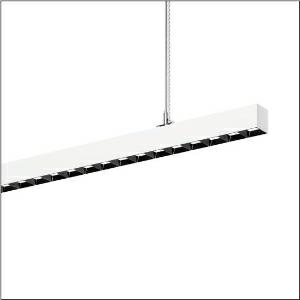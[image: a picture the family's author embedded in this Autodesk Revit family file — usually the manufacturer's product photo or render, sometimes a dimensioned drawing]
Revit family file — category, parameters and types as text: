
# Revit family: silica_r__21_51mx32tat7w_976d
name_source: partatom
category: Lighting Fixtures
units: mm (PartAtom-declared; Revit-internal decimal feet)

## family parameters
Cut with Voids When Loaded = No
Host = Face
Light Source = No
Part Type = Normal
Room Calculation Point = No
Round Connector Dimension = Use Diameter
Shared = No

## types (1)
- --- (1 x LED, 6220 lm, 53.4 W, 6500K)
    Apparent Load = 53 VA
    CIE Flux Codes = 84 99 100 60 100
    Color Rendering = 80
    Color Temperature = 6500K
    Default Elevation = 1800 mm
    Description = Silica® 21, office luminaire, primary light control with darklight reflector, of PMMA, black, CAT 2 (L<= 3000cd/m²), light emission: direct/indirect distribution, primary light characteristic: symmetric, installation type: suspended mounting, LED, rated luminous flux: 6.220lm, luminous efficacy: 111lm/W, light colour: 8tw, colour temperature: 2700..6500K, control gear: ECG DALI, with terminal, 3+2-pole, max. 2.5mm², mains connection: 220..240V, AC, 50/60Hz, rated input power: 56.1W, luminaire housing, of aluminium, traffic white (RAL 9016), length: 1.204mm, width: 53mm, height: 53mm, protection rating (complete): IP20, insulation class (complete): insulation class I (protective earthing), certification: CE, permissible operating ambient temperature: 0..+35°C, standard: EN 50419, packaging unit: 1 piece
    Height = 53 mm
    Lamp = 1 x LED
    Lamp Light Flux = 6220 lm
    Lamp Power = 53.4 W
    Lamp count = 1
    Length = 1204 mm
    Luminous efficacy = 116 lm/W
    Manufacturer = Siteco
    ModVariant = No
    Model = 51MX32TAT7W
    Mounting Place = Ceiling
    Mounting Type = Pendant
    Number of Poles = 1
    OnlyDefault = Yes
    Power Factor = 1
    Product Name = Silica® 21
    Product group = office luminaire | ceiling pendant
    ProductGroupID = 905
    Protection Class = Protection class I
    Protection Degree = IP 20
    RLX_Detail_Level = 1
    RlxData = <blob elided: 40361 chars, md5=967ce4cf>
    Socket = socket
    Standby Power = 0 W
    System Light Flux = 6220 lm
    System Power = 53 W
    Type Comments = individual setting
    Type Image = l_1251637.jpg
    URL = http://relux.com
    VarID = @adj_046053
    Voltage = 0 V
    Weight = 0.00 kg
    Width = 53 mm

## geometry (parser evidence)
native form markers: Blend x4, Sweep x11
no freeform markers — native parametric forms only
